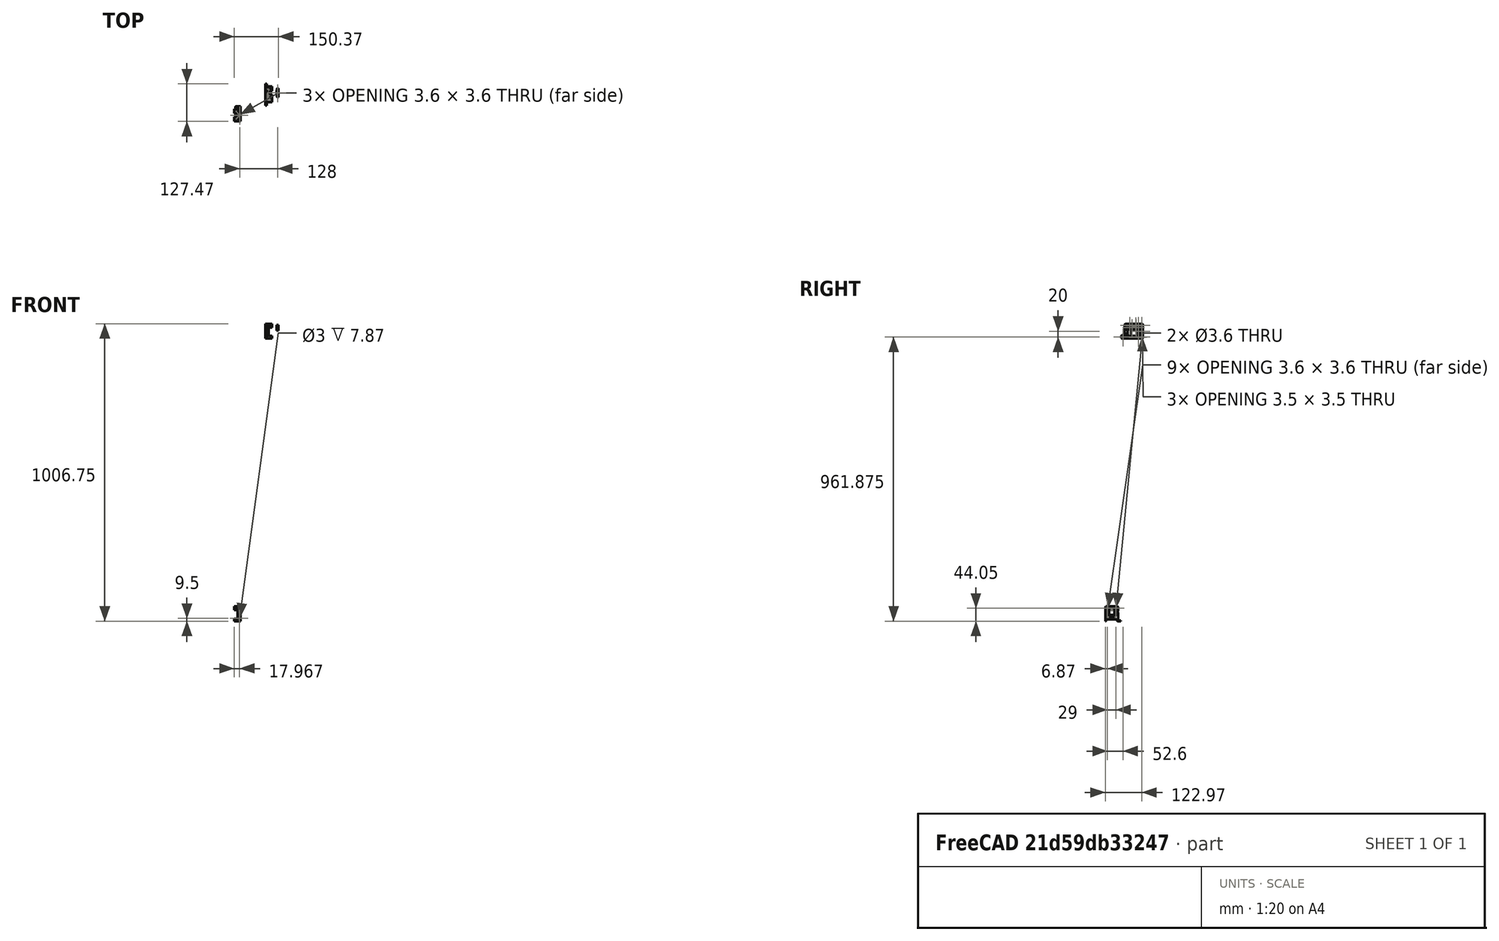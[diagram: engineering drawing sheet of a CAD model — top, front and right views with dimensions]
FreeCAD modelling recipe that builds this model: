
FCSTD DOCUMENT  (FreeCAD 0.19R24291 (Git))
Label: REMIX_BASE
License: All rights reserved
LicenseURL: http://en.wikipedia.org/wiki/All_rights_reserved
objects: Part::Feature×3, Part::Fillet×3, App::Part×1, Part::Refine×1, Part::Box×1, Part::Cut×1, Part::Chamfer×1
note: 10 computed .brp shape members not serialized (recipe doc carries the construction recipe); baked Part::Feature solids carry a one-line shape summary decoded from their .brp

FEATURE [Part::Feature] Part__Feature  label="Mount"
  Placement = pos=(-3,-1.39e-14,0) rot=(0,0,1;0rad)
  shape: bbox 7.3 x 31.16 x 19.26 mm, 34 faces (baked)
FEATURE [Part::Feature] Part__Feature001  label="Cover"
  Placement = pos=(-5.36765,-1.39e-14,0) rot=(0,0,1;0rad)
  shape: bbox 24.56 x 73.39 x 49.76 mm, 159 faces (baked)
FEATURE [Part::Feature] Part__Feature002  label="Back"
  Placement = pos=(-5.36765,-1.39e-14,0) rot=(0,0,1;0rad)
  shape: bbox 23.79 x 62.51 x 49.76 mm, 128 faces (baked)
FEATURE [App::Part] X5S_Hotend
  Group = -> [Part__Feature,Part__Feature001,Part__Feature002]
  Origin = -> Origin
FEATURE [Part::Refine] Part__Feature002001  label="Back001"
  Placement = pos=(-128,-75.6,-957) rot=(0,0,1;0rad)
  Source = -> Part__Feature002
FEATURE [Part::Box] Box  label="Cubo"
  AttacherType = Attacher::AttachEngine3D
  Height = 60
  Length = 50
  Placement = pos=(0,-30,0) rot=(0,0,1;0rad)
  Width = 30
FEATURE [Part::Cut] Cut
  Base = -> Part__Feature002001
  Tool = -> Box
FEATURE [Part::Chamfer] Chamfer
  Base = -> Cut
  Edges = 1 edges r=2: [Edge48]
FEATURE [Part::Fillet] Fillet
  Base = -> Chamfer
  Edges = 1 edges r=2: [Edge314]
FEATURE [Part::Fillet] Fillet001
  Base = -> Fillet
  Edges = 1 edges r=2: [Edge11]
FEATURE [Part::Fillet] Fillet002
  Base = -> Fillet001
  Edges = 1 edges r=3: [Edge30]
